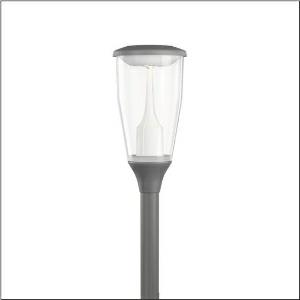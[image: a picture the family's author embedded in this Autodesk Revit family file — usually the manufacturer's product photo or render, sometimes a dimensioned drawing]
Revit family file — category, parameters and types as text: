
# Revit family: dl_11_iq___p1_0a_5xa5575ff14hp00022_3c96
name_source: partatom
category: Lighting Fixtures
units: mm (PartAtom-declared; Revit-internal decimal feet)

## family parameters
Cut with Voids When Loaded = No
Host = Face
Light Source = No
Part Type = Normal
Room Calculation Point = No
Round Connector Dimension = Use Diameter
Shared = No

## types (1)
- --- (1 x LED, 4780 lm, 33.6 W, 3000K)
    Apparent Load = 34 VA
    CIE Flux Codes = 33 63 91 94 100
    Color Rendering = 70
    Color Temperature = 3000K
    Default Elevation = 1800 mm
    Description = DL 11 iQ, mast luminaire, Module 540 iQ-SR, primary light control with 3 zone facetted reflector, of plastic, silver coated, highly specular, structured, primary optical cover: cover, of PMMA, transparent, light distribution: P1.0a, light emission: direct distribution, primary light characteristic: asymmetric, installation type: post-top, LED, High Power LED, light colour: 730, colour temperature: 3000K, control gear: iQ Street-Remote, control: Street-Remote, Auto-Match, Temp-Guard, Lumen-Switch, Night-Set, Smart-Wire, Light-Fading, Desk-Remote (wireless, voltage-free reading and setting of iQ features in the workshop via application-optimized NFC function/RFID function), optimised constant luminous flux control (CLO 2.0), mains connection: 220..240V, AC, 50/60Hz, connection cable pre-assembled, cable length: 5,5m, wiring characteristics: H07RN-F, 5-core, 1.5mm², start of lifetime: 34W, end of service life: 36W, luminaire housing, upper part, of diecast aluminium, coated, Siteco® metallic grey (DB 702S), spigot size: 76mm (post-top), mounting height: 3..5m, post-top mast mounting element, of diecast aluminium, coated, Siteco® metallic grey (DB 702S), Module 540 iQ-SR, traffic white (RAL 9016), equipment: Power, protection rating (complete): IP66, insulation class (complete): insulation class II (safety insulation), certification: CE, ENEC, ENEC+, VDE, impact resistance: IK07, packaging unit: 1 piece

Light Distribution: P1.0a
    Height = 665 mm
    Lamp = 1 x LED
    Lamp Light Flux = 4780 lm
    Lamp Power = 33.6 W
    Lamp count = 1
    Length = 334 mm
    Luminous efficacy = 142 lm/W
    Manufacturer = Siteco
    ModVariant = No
    Model = 5XA5575FF14HP00022
    Number of Poles = 1
    OnlyDefault = Yes
    Power Factor = 1
    Product Name = DL 11 iQ | P1.0a
    Product group = mast luminaire | pylon top
    ProductGroupID = 6100
    Protection Class = Protection class II
    Protection Degree = IP 66
    RLX_Detail_Level = 1
    RLX_Emergency_Light_Flux = 0 lm
    RLX_Emergency_Type = 0
    RLX_Emergency_Type_DB = No
    RlxData = <blob elided: 105121 chars, md5=a8d79b7f>
    Socket = socket
    Standby Power = 0 W
    System Light Flux = 4780 lm
    System Power = 34 W
    Type Comments = factory setting: luminous flux: 100 % | dim-lin: 254 | 695 mA
    Type Image = l_1258354.jpg
    URL = http://relux.com
    VarID = @adj_053253
    Voltage = 0 V
    Weight = 0.00 kg
    Width = 0 mm  [stored 0 ft]

note: [stored X ft] marks values corroborated as IEEE doubles in the binary element streams (Revit-internal decimal feet)

## geometry (parser evidence)
native form markers: Blend x4, Sweep x9
no freeform markers — native parametric forms only
